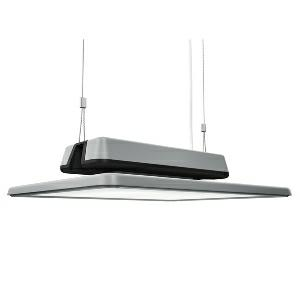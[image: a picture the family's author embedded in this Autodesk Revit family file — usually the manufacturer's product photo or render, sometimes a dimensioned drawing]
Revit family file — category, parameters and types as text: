
# Revit family: acaneo_-_hial_30000_850_n_ea_00734120_71ff
name_source: partatom
category: Lighting Fixtures
units: mm (PartAtom-declared; Revit-internal decimal feet)

## family parameters
Cut with Voids When Loaded = No
Host = Face
Light Source = No
Part Type = Normal
Room Calculation Point = No
Round Connector Dimension = Use Diameter
Shared = No

## types (1)
- ACANEO - HIAL 30000/850/N/EA (1 x LED, 33000 lm, 5000K)
    Apparent Load = 206 VA
    Approval mark = CE
    CIE Flux Codes = 84 97 100 100 100
    Color Rendering = 80-89
    Color Temperature = 5000K
    Control Gear = Electronic ballast
    Default Elevation = 1800 mm
    Description = HIAL 30000/850/N/EA|High bay luminaire|light source: LED|work equipment: Electronic ballast|connected load: 220-240 V, 50/60 Hz|Power consumption: approx. 206 W|power factor: approx. 0,973|luminous flux: 33000 lm|luminous efficacy: 160 lm/W|colour temperature: Cold white, ca. 5000 K|color rendering index (CRI): >= 80|chromaticity tolerance:  3 SDCM|System of protection: IP 65|class of protection: I|technology: Switchable|luminaire body|material: Aluminium|surface: Powder coatet|colour: White aluminium|lamp cover: Acrylic (PMMA), Clear|weight (net): approx. 10.8 kg|mains lead: Built-in plug RST 25i3 Einbau|Fastening: Available separately|Accessory: Junction box (RST 2013)|minimum ambient temperature: -30 ░C|maximum ambient temperature: 50 ░C|glare control: Optics|unified glare rating(4H 8H): <=  22|
    Frequency = 50 Hz, 60 Hz
    Height = 125 mm
    Lamp = 1 x LED
    Lamp Light Flux = 33000 lm
    Lamp count = 1
    Length = 585 mm
    Luminous efficacy = 160 lm/W
    Manufacturer = Waldmann
    ModVariant = No
    Model = 00734120
    Mounting Place = Ceiling
    Mounting Type = Pendant
    Number of Poles = 1
    OnlyDefault = Yes
    Power Factor = 1
    Product Name = ACANEO - HIAL 30000/850/N/EA
    Product group = High bay luminaire (industry)
    ProductGroupID = 901
    Protection Class = Protection class I
    Protection Degree = IP 65
    RLX_Detail_Level = 1
    RLX_Emergency_Light_Flux = 0 lm
    RLX_Emergency_Type = 0
    RLX_Emergency_Type_DB = No
    RlxData = <blob elided: 29805 chars, md5=43f267c3>
    Socket = socket
    Standby Power = 0 W
    System Light Flux = 32999 lm
    System Power = 206 W
    Type Comments = Product without accessories
    Type Image = acaneo-hial.jpg
    URL = http://relux.com
    VarID = ---
    Voltage = 230 V
    Voltage Range = 110-120 V, 220-240 V
    Weight = 0.00 kg
    Width = 480 mm

## geometry (parser evidence)
native form markers: Blend x4, Sweep x10
no freeform markers — native parametric forms only
